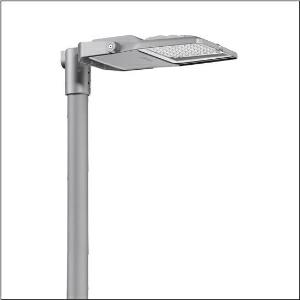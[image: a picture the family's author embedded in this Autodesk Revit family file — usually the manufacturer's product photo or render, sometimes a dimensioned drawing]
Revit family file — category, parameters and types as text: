
# Revit family: floodlight_fl_21_iq_mini___pl61_5xa7771c4c3a_1011
name_source: partatom
category: Lighting Fixtures
units: mm (PartAtom-declared; Revit-internal decimal feet)

## family parameters
Cut with Voids When Loaded = No
Host = Face
Light Source = No
Part Type = Normal
Room Calculation Point = No
Round Connector Dimension = Use Diameter
Shared = No

## types (1)
- --- (1 x LED, 12490 lm, 87.2 W, 4000K)
    Apparent Load = 87 VA
    CIE Flux Codes = 33 65 98 100 100
    Color Rendering = 70
    Color Temperature = 4000K
    Default Elevation = 1800 mm
    Description = Floodlight FL 21 iQ mini, floodlight, primary light control with lens, of PMMA, primary optical cover: protective disc, of toughened safety glass, transparent, light distribution: PL61, light emission: direct distribution, installation type: surface-mounted, LED, High Power LED, rated luminous flux: 12.490lm, luminous efficacy: 143lm/W, light colour: 740, colour temperature: 4000K, control: Auto-Match, Temp-Guard, Lumen-Switch, Night-Set, Smart-Wire, Light-Fading, Desk-Remote (wireless, voltage-free reading and setting of iQ features in the workshop via application-optimized NFC function/RFID function), optimised constant luminous flux control (CLO 2.0), with terminal, 6-pole, mains connection: 220..240V, AC, 50/60Hz, start of lifetime: 87W, end of service life: 92W, reduction: 40W, luminaire housing, of diecast aluminium, powder-coated, Siteco® metallic grey (DB 702S), corrosivity category C5 mid according to DIN EN ISO 12944, sealing non-destructively replaceable, please order mast flange separately, mast bracket, of steel, galvanised, powder-coated, Siteco® metallic grey (DB 702S), protection rating (complete): IP66, insulation class (complete): insulation class II (safety insulation), certification: CE, ENEC, VDE, protection symbol: D, impact resistance: IK08, permissible operating ambient temperature: -40..+40°C, permissible operating ambient temperature for outdoor applications: -40..+50°C, standard: DIN EN 12944, LABS conformity tested according to VDMA 24364:2018-05, packaging unit: 1 piece

Light Distribution: PL61
    Height = 70 mm
    Lamp = 1 x LED
    Lamp Light Flux = 12490 lm
    Lamp Power = 87.2 W
    Lamp count = 1
    Length = 485 mm
    Luminous efficacy = 143 lm/W
    Manufacturer = Siteco
    ModVariant = No
    Model = 5XA7771C4C3A
    Number of Poles = 1
    OnlyDefault = Yes
    Power Factor = 1
    Product Name = Floodlight FL 21 iQ mini | PL61
    Product group = floodlight | pylon annexe
    ProductGroupID = 6200
    Protection Class = Protection class II
    Protection Degree = IP 66
    RLX_Detail_Level = 1
    RLX_Emergency_Light_Flux = 0 lm
    RLX_Emergency_Type = 0
    RLX_Emergency_Type_DB = No
    RlxData = <blob elided: 101393 chars, md5=89778a96>
    Socket = socket
    Standby Power = 0 W
    System Light Flux = 12490 lm
    System Power = 87 W
    Type Comments = factory setting: luminous flux: 100 % | dim-lin: 254 | 456 mA
    Type Image = l_1007125.jpg
    URL = http://relux.com
    VarID = @adj_144297
    Voltage = 0 V
    Weight = 0.00 kg
    Width = 337 mm

## geometry (parser evidence)
native form markers: Blend x4, Sweep x12
no freeform markers — native parametric forms only
